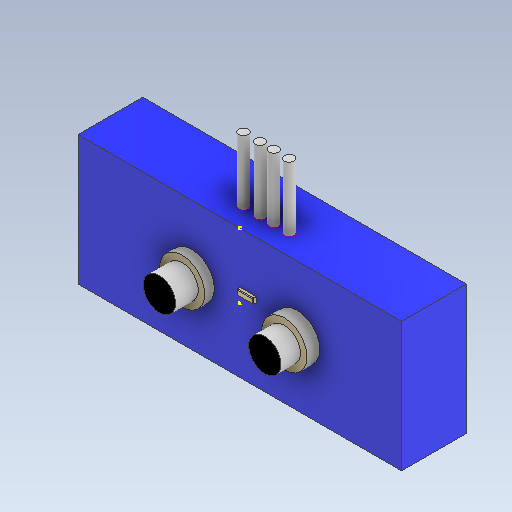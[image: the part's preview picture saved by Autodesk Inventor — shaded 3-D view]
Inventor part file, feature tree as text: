
AUTODESK INVENTOR PART (.ipt)
format: ipt  version: 2021 (Build 250183000, 183)  size: 170,496 bytes
history: native  units: mm
features: extrude x8, sketch x3, fillet x1
ambient origin geometry x8: Origin, YZ Plane, XZ Plane, XY Plane, X Axis, Y Axis, Z Axis, Center Point
bodies: Solid1 (feature_tree)
feature tree (12):
  sketch  "Sketch1"  dims[d0=7.0mm d1=7.0mm]
  extrude  "Extrusion1"  Depth=7.0mm
  extrude  "Extrusion2"  Depth=1.5mm TaperAngle=0.0deg
  extrude  "Extrusion3"  Depth=0.5mm TaperAngle=0.0deg
  extrude  "Extrusion4"  Depth=0.1mm
  fillet  "Fillet1"  Radius=5.0mm
  extrude  "Extrusion5"  Depth=5.0mm
  extrude  "Extrusion6"  Depth=5.0mm TaperAngle=0.0deg
  sketch  "Sketch3"  dims[d2=10.0mm d3=0.0mm d4=1.5mm d5=0.0mm]
  extrude  "Extrusion8"  Depth=5.0mm TaperAngle=0.0deg
  extrude  "Extrusion9"  Depth=1.5mm
  sketch  "Sketch4"  dims[d6=2.0mm d7=0.0mm d8=0.5mm d9=0.0mm d10=0.1mm d11=5.0mm d12=5.0mm d13=5.0mm d14=0.0mm d15=5.0mm d16=0.0mm d19=1.5mm d20=1.5mm d21=1.5mm d22=1.5mm d24=10.0mm d25=0.0mm d26=10.0mm d27=0.0mm d28=50.0mm d29=20.0mm]
